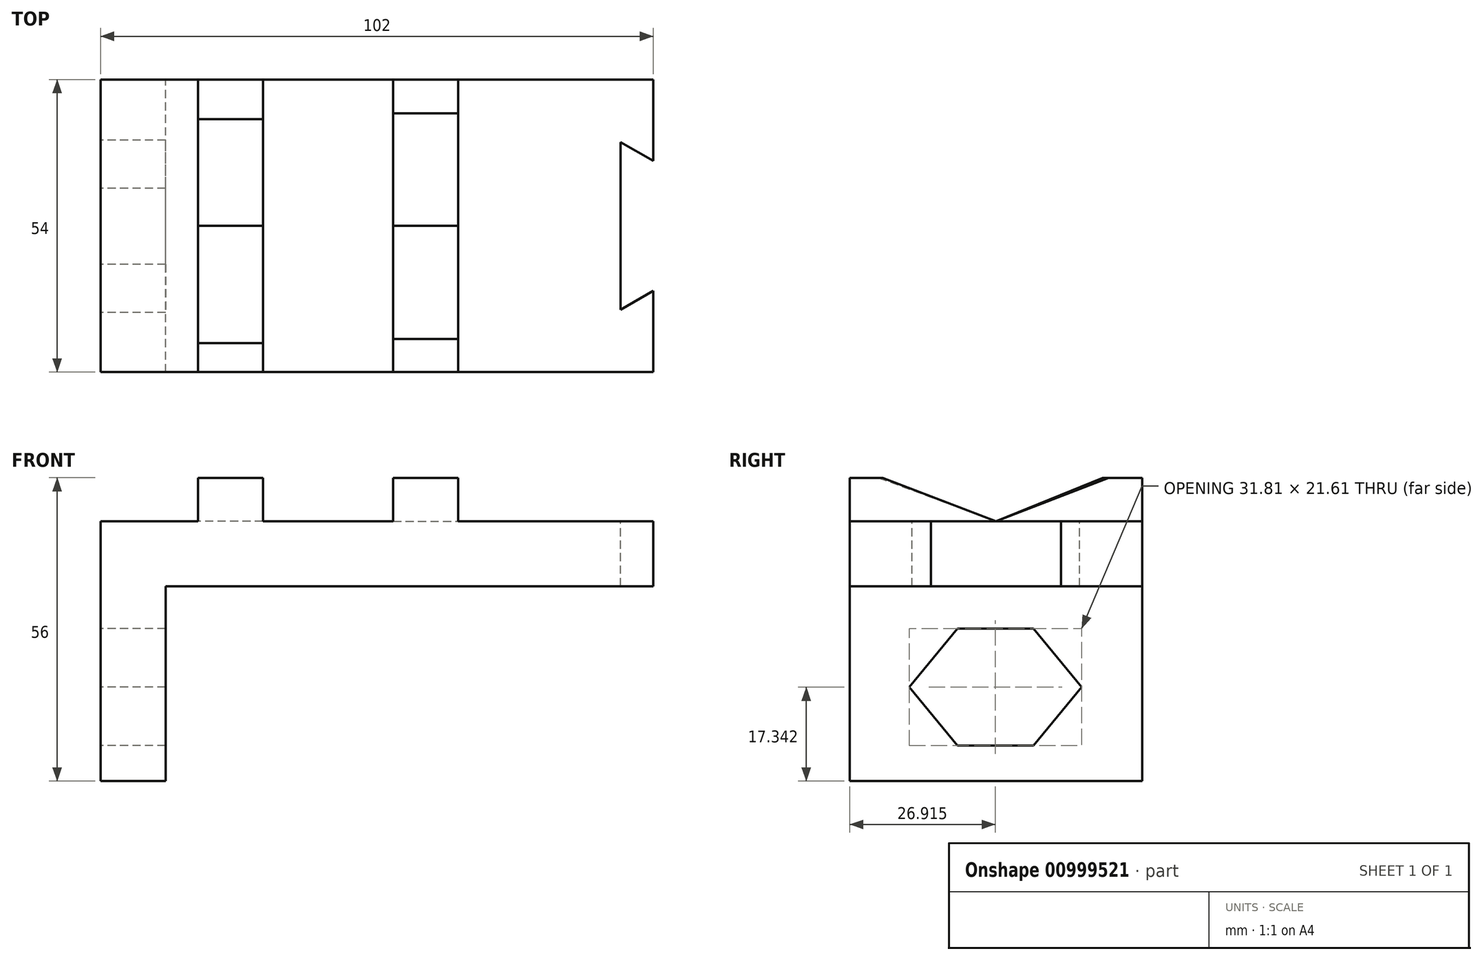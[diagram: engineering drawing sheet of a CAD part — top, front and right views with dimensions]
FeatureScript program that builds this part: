
annotation { "Feature Type Name" : "Feature", "Feature Type Description" : "" }
export const myFeature = defineFeature(function(context is Context, id is Id, definition is map)
    precondition{}
    {
        {
            var Q0;
            Q0=qCreatedBy(makeId("Right.planeOp"),FACE);
            var sketch = newSketch(context, id + "F0", { "sketchPlane" : qUnion([Q0])});
            skLineSegment(sketch, "E0", {"start": v(22.95, 32.94) * mm, "end": v(22.95, -23.06) * mm});
            skLineSegment(sketch, "E1", {"start": v(22.95, -23.06) * mm, "end": v(-31.05, -23.06) * mm});
            skLineSegment(sketch, "E2", {"start": v(-31.05, -23.06) * mm, "end": v(-31.05, 32.94) * mm});
            skLineSegment(sketch, "E3", {"start": v(-31.05, 32.94) * mm, "end": v(22.95, 32.94) * mm});
            skSolve(sketch);
        }
        {
            var Q0;
            Q0 = qSketchRegion(id + "F0", true);
            extrude(context, id + "F1", {"entities" : qUnion([Q0]), "surfaceOperationType" : NewSurfaceOperationType.ADD, "depth" : 102 * mm, "offsetDistance" : 25 * mm});
        }
        {
            var Q0;
            Q0=makeQuery(id+"F1.opExtrude","SWEPT_FACE",FACE,{"disambiguationData":[OSD([sQuery(id+"F0.wireOp",EDGE,"E0")])]});
            var sketch = newSketch(context, id + "F2", { "sketchPlane" : qUnion([Q0])});
            skLineSegment(sketch, "E4", {"start": v(0, -23.06) * mm, "end": v(-12, -23.06) * mm});
            skLineSegment(sketch, "E5", {"start": v(-12, -23.06) * mm, "end": v(-12, 12.94) * mm});
            skLineSegment(sketch, "E6", {"start": v(-12, 12.94) * mm, "end": v(-102, 12.94) * mm});
            skLineSegment(sketch, "E7", {"start": v(-102, 12.94) * mm, "end": v(-102, 24.94) * mm});
            skLineSegment(sketch, "E8", {"start": v(-102, 24.94) * mm, "end": v(0, 24.94) * mm});
            skLineSegment(sketch, "E9", {"start": v(0, 24.94) * mm, "end": v(0, 32.94) * mm});
            skLineSegment(sketch, "E10", {"start": v(-102, 12.94) * mm, "end": v(-102, -23.06) * mm});
            skLineSegment(sketch, "E11", {"start": v(-102, -23.06) * mm, "end": v(-12, -23.06) * mm});
            skSolve(sketch);
        }
        {
            var Q0;
            Q0=makeQuery(id+"F2.imprint","IMPRINT",FACE,{"disambiguationData":[TD([[makeQuery(id+"F2.imprint","IMPRINT",EDGE,{"derivedFrom":sQuery(id+"F2.wireOp",EDGE,"E5")}),1.0]])]});
            extrude(context, id + "F3", {"entities" : qUnion([Q0]), "operationType" : NewBodyOperationType.REMOVE, "oppositeDirection" : true, "depth" : 59.1 * mm, "offsetDistance" : 25 * mm});
        }
        {
            var Q0;
            Q0=makeQuery(id+"F1.opExtrude","CAP_FACE",FACE,{"disambiguationData":[OSD([sQuery(id+"F0.wireOp",EDGE,"E0"),sQuery(id+"F0.wireOp",EDGE,"E1"),sQuery(id+"F0.wireOp",EDGE,"E2"),sQuery(id+"F0.wireOp",EDGE,"E3")])],"isStart":true});
            var sketch = newSketch(context, id + "F4", { "sketchPlane" : qUnion([Q0])});
            skLineSegment(sketch, "E12", {"start": v(-22.95, 32.94) * mm, "end": v(-22.95, 24.94) * mm});
            skLineSegment(sketch, "E13", {"start": v(-22.95, 24.94) * mm, "end": v(31.05, 24.94) * mm});
            skLineSegment(sketch, "E14", {"start": v(31.05, 24.94) * mm, "end": v(31.05, 32.94) * mm});
            skLineSegment(sketch, "E15", {"start": v(31.05, 32.94) * mm, "end": v(-22.95, 32.94) * mm});
            skSolve(sketch);
        }
        {
            var Q0;
            {var subQ0=sQuery(id+"F4.wireOp",EDGE,"E13");Q0=makeQuery(id+"F4.imprint","IMPRINT",FACE,{"disambiguationData":[TD([[makeQuery(id+"F4.imprint","IMPRINT",EDGE,{"derivedFrom":subQ0}),-1.0]])]});}
            var sketch = newSketch(context, id + "F5", { "sketchPlane" : qUnion([Q0])});
            skLineSegment(sketch, "E16", {"start": v(11.14, -16.52) * mm, "end": v(-2.86, -16.52) * mm});
            skLineSegment(sketch, "E17", {"start": v(11.14, -16.52) * mm, "end": v(20.04, -5.72) * mm});
            skLineSegment(sketch, "E18", {"start": v(20.04, -5.72) * mm, "end": v(11.14, 5.08) * mm});
            skLineSegment(sketch, "E19", {"start": v(11.14, 5.08) * mm, "end": v(-2.86, 5.08) * mm});
            skLineSegment(sketch, "E20", {"start": v(-2.86, 5.08) * mm, "end": v(-11.77, -5.72) * mm});
            skLineSegment(sketch, "E21", {"start": v(-11.77, -5.72) * mm, "end": v(-2.86, -16.52) * mm});
            skSolve(sketch);
        }
        {
            var Q0;
            Q0=makeQuery(id+"F5.imprint","IMPRINT",FACE,{"disambiguationData":[TD([[makeQuery(id+"F5.imprint","IMPRINT",EDGE,{"derivedFrom":sQuery(id+"F5.wireOp",EDGE,"E16")}),-1.0]])]});
            extrude(context, id + "F6", {"entities" : qUnion([Q0]), "operationType" : NewBodyOperationType.REMOVE, "oppositeDirection" : true, "depth" : 25 * mm, "offsetDistance" : 25 * mm});
        }
        {
            var Q0;
            Q0=makeQuery(id+"F1.opExtrude","SWEPT_FACE",FACE,{"disambiguationData":[OSD([sQuery(id+"F0.wireOp",EDGE,"E3")])]});
            var sketch = newSketch(context, id + "F7", { "sketchPlane" : qUnion([Q0])});
            skLineSegment(sketch, "E22", {"start": v(0, 22.95) * mm, "end": v(18, 22.95) * mm});
            skLineSegment(sketch, "E23", {"start": v(18, 22.95) * mm, "end": v(18, -31.05) * mm});
            skLineSegment(sketch, "E24", {"start": v(18, -31.05) * mm, "end": v(0, -31.05) * mm});
            skLineSegment(sketch, "E25", {"start": v(0, -31.05) * mm, "end": v(0, 22.95) * mm});
            skSolve(sketch);
        }
        {
            var Q0;
            Q0=makeQuery(id+"F7.imprint","IMPRINT",FACE,{"disambiguationData":[TD([[makeQuery(id+"F7.imprint","IMPRINT",EDGE,{"derivedFrom":sQuery(id+"F7.wireOp",EDGE,"E22")}),1.0]])]});
            extrude(context, id + "F8", {"entities" : qUnion([Q0]), "operationType" : NewBodyOperationType.REMOVE, "oppositeDirection" : true, "depth" : 8 * mm, "offsetDistance" : 25 * mm});
        }
        {
            var Q0;
            Q0=makeQuery(id+"F1.opExtrude","SWEPT_FACE",FACE,{"disambiguationData":[OSD([sQuery(id+"F0.wireOp",EDGE,"E3")])]});
            var sketch = newSketch(context, id + "F9", { "sketchPlane" : qUnion([Q0])});
            skLineSegment(sketch, "E26", {"start": v(18, 22.95) * mm, "end": v(30, 22.95) * mm});
            skLineSegment(sketch, "E27", {"start": v(30, 22.95) * mm, "end": v(30, -31.05) * mm});
            skLineSegment(sketch, "E28", {"start": v(30, -31.05) * mm, "end": v(18, -31.05) * mm});
            skLineSegment(sketch, "E29", {"start": v(30, 22.95) * mm, "end": v(54, 22.95) * mm});
            skLineSegment(sketch, "E30", {"start": v(54, 22.95) * mm, "end": v(54, -31.05) * mm});
            skLineSegment(sketch, "E31", {"start": v(54, -31.05) * mm, "end": v(30, -31.05) * mm});
            skSolve(sketch);
        }
        {
            var Q0;
            Q0=makeQuery(id+"F9.imprint","IMPRINT",FACE,{"disambiguationData":[TD([[makeQuery(id+"F9.imprint","IMPRINT",EDGE,{"derivedFrom":sQuery(id+"F9.wireOp",EDGE,"E27")}),1.0]])]});
            extrude(context, id + "F10", {"entities" : qUnion([Q0]), "operationType" : NewBodyOperationType.REMOVE, "oppositeDirection" : true, "depth" : 8 * mm, "offsetDistance" : 25 * mm});
        }
        {
            var Q0;
            {var subQ1=sQuery(id+"F0.wireOp",EDGE,"E3");Q0=makeQuery(id+"F10.boolean.opBoolean","SPLIT",FACE,{"disambiguationData":[TD([makeQuery(id+"F10.opExtrude","SWEPT_FACE",FACE,{"disambiguationData":[OSD([sQuery(id+"F9.wireOp",EDGE,"E30")])]})])],"derivedFrom":makeQuery(id+"F1.opExtrude","SWEPT_FACE",FACE,{"disambiguationData":[OSD([subQ1])]})});}
            var sketch = newSketch(context, id + "F11", { "sketchPlane" : qUnion([Q0])});
            skLineSegment(sketch, "E32", {"start": v(54, 22.95) * mm, "end": v(66, 22.95) * mm});
            skLineSegment(sketch, "E33", {"start": v(66, 22.95) * mm, "end": v(66, -31.05) * mm});
            skLineSegment(sketch, "E34", {"start": v(66, -31.05) * mm, "end": v(54, -31.05) * mm});
            skLineSegment(sketch, "E35", {"start": v(54, -31.05) * mm, "end": v(54, 22.95) * mm});
            skLineSegment(sketch, "E36", {"start": v(66, -31.05) * mm, "end": v(102, -31.05) * mm});
            skLineSegment(sketch, "E37", {"start": v(102, -31.05) * mm, "end": v(102, 22.95) * mm});
            skLineSegment(sketch, "E38", {"start": v(102, 22.95) * mm, "end": v(66, 22.95) * mm});
            skSolve(sketch);
        }
        {
            var Q0;
            Q0=makeQuery(id+"F11.imprint","IMPRINT",FACE,{"disambiguationData":[TD([[makeQuery(id+"F11.imprint","IMPRINT",EDGE,{"derivedFrom":sQuery(id+"F11.wireOp",EDGE,"E33")}),1.0]])]});
            extrude(context, id + "F12", {"entities" : qUnion([Q0]), "operationType" : NewBodyOperationType.REMOVE, "oppositeDirection" : true, "depth" : 8 * mm, "offsetDistance" : 25 * mm});
        }
        {
            var Q0;
            Q0=makeQuery(id+"F12.boolean.opBoolean","COPY",FACE,{"derivedFrom":makeQuery(id+"F12.opExtrude","SWEPT_FACE",FACE,{"disambiguationData":[OSD([sQuery(id+"F11.wireOp",EDGE,"E33")])]})});
            var sketch = newSketch(context, id + "F13", { "sketchPlane" : qUnion([Q0])});
            skLineSegment(sketch, "E39", {"start": v(-4.05, 32.94) * mm, "end": v(-4.05, 24.94) * mm});
            skLineSegment(sketch, "E40", {"start": v(-24.92, 32.94) * mm, "end": v(-4.05, 24.94) * mm});
            skLineSegment(sketch, "E41", {"start": v(16.72, 32.94) * mm, "end": v(-4.05, 24.94) * mm});
            skLineSegment(sketch, "E42", {"start": v(-24.92, 32.94) * mm, "end": v(16.72, 32.94) * mm});
            skSolve(sketch);
        }
        {
            var Q0;
            {var subQ0=sQuery(id+"F13.wireOp",EDGE,"E39");Q0=makeQuery(id+"F13.imprint","IMPRINT",FACE,{"disambiguationData":[TD([[makeQuery(id+"F13.imprint","IMPRINT",EDGE,{"derivedFrom":subQ0}),1.0]])]});}
            extrude(context, id + "F14", {"entities" : qUnion([Q0]), "operationType" : NewBodyOperationType.REMOVE, "oppositeDirection" : true, "depth" : 12 * mm, "offsetDistance" : 25 * mm});
        }
        {
            var Q0;
            {var subQ0=sQuery(id+"F11.wireOp",EDGE,"E33");var subQ1=makeQuery(id+"F12.boolean.opBoolean","COPY",FACE,{"derivedFrom":makeQuery(id+"F12.opExtrude","SWEPT_FACE",FACE,{"disambiguationData":[OSD([subQ0])]})});Q0=makeQuery(id+"F14.boolean.opBoolean","SPLIT",FACE,{"disambiguationData":[TD([makeQuery(id+"F1.opExtrude","SWEPT_FACE",FACE,{"disambiguationData":[OSD([sQuery(id+"F0.wireOp",EDGE,"E2")])]})])],"derivedFrom":subQ1});}
            var sketch = newSketch(context, id + "F15", { "sketchPlane" : qUnion([Q0])});
            skLineSegment(sketch, "E43", {"start": v(-24.92, 32.94) * mm, "end": v(-4.05, 24.94) * mm});
            skLineSegment(sketch, "E44", {"start": v(-4.05, 24.94) * mm, "end": v(-4.05, 32.94) * mm});
            skLineSegment(sketch, "E45", {"start": v(-4.05, 32.94) * mm, "end": v(-24.92, 32.94) * mm});
            skSolve(sketch);
        }
        {
            var Q0;
            Q0=makeQuery(id+"F15.imprint","IMPRINT",FACE,{"disambiguationData":[TD([[makeQuery(id+"F15.imprint","IMPRINT",EDGE,{"derivedFrom":sQuery(id+"F15.wireOp",EDGE,"E43")}),1.0]])]});
            extrude(context, id + "F16", {"entities" : qUnion([Q0]), "operationType" : NewBodyOperationType.REMOVE, "oppositeDirection" : true, "depth" : 25 * mm, "offsetDistance" : 25 * mm});
        }
        {
            var Q0;
            Q0=makeQuery(id+"F4.imprint","IMPRINT",FACE,{"disambiguationData":[TD([[makeQuery(id+"F4.imprint","IMPRINT",EDGE,{"derivedFrom":sQuery(id+"F4.wireOp",EDGE,"E12")}),1.0]])]});
            var sketch = newSketch(context, id + "F17", { "sketchPlane" : qUnion([Q0])});
            skLineSegment(sketch, "E46", {"start": v(26.29, 33.15) * mm, "end": v(32.29, 33.15) * mm});
            skLineSegment(sketch, "E47", {"start": v(-22.85, 33.43) * mm, "end": v(-16.85, 33.43) * mm});
            skLineSegment(sketch, "E48", {"start": v(-16.85, 33.43) * mm, "end": v(4.06, 24.94) * mm});
            skLineSegment(sketch, "E49", {"start": v(26.29, 33.15) * mm, "end": v(4.06, 24.94) * mm});
            skLineSegment(sketch, "E50", {"start": v(-16.85, 33.43) * mm, "end": v(26.29, 33.15) * mm});
            skSolve(sketch);
        }
        {
            var Q0;
            Q0 = qSketchRegion(id + "F17", true);
            extrude(context, id + "F18", {"entities" : qUnion([Q0]), "operationType" : NewBodyOperationType.REMOVE, "oppositeDirection" : true, "depth" : 42.4 * mm, "offsetDistance" : 25 * mm});
        }
        {
            var Q0;
            Q0=makeQuery(id+"F12.boolean.opBoolean","COPY",FACE,{"derivedFrom":makeQuery(id+"F12.opExtrude","CAP_FACE",FACE,{"disambiguationData":[OSD([sQuery(id+"F11.wireOp",EDGE,"E33"),sQuery(id+"F11.wireOp",EDGE,"E36"),sQuery(id+"F11.wireOp",EDGE,"E37"),sQuery(id+"F11.wireOp",EDGE,"E38")])],"isStart":false})});
            var sketch = newSketch(context, id + "F19", { "sketchPlane" : qUnion([Q0])});
            skLineSegment(sketch, "E51", {"start": v(102, -31.05) * mm, "end": v(96, -31.05) * mm});
            skLineSegment(sketch, "E52", {"start": v(96, -31.05) * mm, "end": v(102, -31.05) * mm});
            skLineSegment(sketch, "E53", {"start": v(102, -31.05) * mm, "end": v(102, -16.05) * mm});
            skLineSegment(sketch, "E54", {"start": v(102, -16.05) * mm, "end": v(102, 7.95) * mm});
            skLineSegment(sketch, "E55", {"start": v(102, 7.95) * mm, "end": v(102, 22.95) * mm});
            skLineSegment(sketch, "E56", {"start": v(102, 22.95) * mm, "end": v(96, 22.95) * mm});
            skLineSegment(sketch, "E57", {"start": v(96, -31.05) * mm, "end": v(96, 22.95) * mm});
            skLineSegment(sketch, "E58", {"start": v(102, 7.95) * mm, "end": v(96, 11.41) * mm});
            skLineSegment(sketch, "E59", {"start": v(102, -16.05) * mm, "end": v(96, -19.51) * mm});
            skSolve(sketch);
        }
        {
            var Q0;
            Q0=makeQuery(id+"F19.imprint","IMPRINT",FACE,{"disambiguationData":[TD([[makeQuery(id+"F19.imprint","IMPRINT",EDGE,{"derivedFrom":sQuery(id+"F19.wireOp",EDGE,"E54")}),1.0]])]});
            extrude(context, id + "F20", {"entities" : qUnion([Q0]), "operationType" : NewBodyOperationType.REMOVE, "oppositeDirection" : true, "depth" : 25 * mm, "offsetDistance" : 25 * mm});
        }
    });
